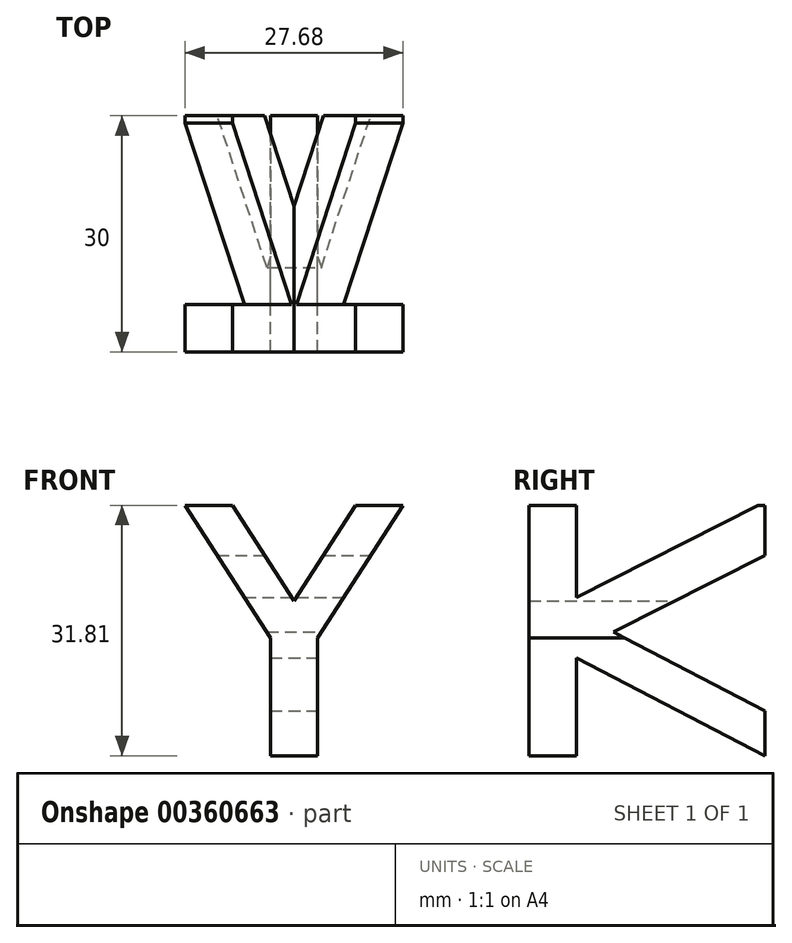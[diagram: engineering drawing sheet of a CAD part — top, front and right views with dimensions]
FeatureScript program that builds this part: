
annotation { "Feature Type Name" : "Feature", "Feature Type Description" : "" }
export const myFeature = defineFeature(function(context is Context, id is Id, definition is map)
    precondition{}
    {
        {
            var Q0;
            Q0=qCreatedBy(makeId("Front.planeOp"),FACE);
            var sketch = newSketch(context, id + "F0", { "sketchPlane" : qUnion([Q0])});
            skLineSegment(sketch, "E0", {"start": v(0, 0) * mm, "end": v(3, 0) * mm});
            skLineSegment(sketch, "E1", {"start": v(3, 0) * mm, "end": v(3, 15) * mm});
            skLineSegment(sketch, "E2", {"start": v(3, 15) * mm, "end": v(13.84, 31.8) * mm});
            skLineSegment(sketch, "E3", {"start": v(13.84, 31.8) * mm, "end": v(7.84, 31.8) * mm});
            skLineSegment(sketch, "E4", {"start": v(7.84, 31.8) * mm, "end": v(0, 19.65) * mm});
            skLineSegment(sketch, "E5.MirrorCS", {"start": v(-7.84, 31.8) * mm, "end": v(0, 19.65) * mm});
            skLineSegment(sketch, "E6.MirrorCS", {"start": v(-13.84, 31.8) * mm, "end": v(-7.84, 31.8) * mm});
            skLineSegment(sketch, "E7.MirrorCS", {"start": v(-3, 15) * mm, "end": v(-13.84, 31.8) * mm});
            skLineSegment(sketch, "E8.MirrorCS", {"start": v(-3, 0) * mm, "end": v(-3, 15) * mm});
            skLineSegment(sketch, "E9.MirrorCS", {"start": v(0, 0) * mm, "end": v(-3, 0) * mm});
            skSolve(sketch);
        }
        {
            var Q0;
            Q0=makeQuery(id+"F0.imprint","IMPRINT",FACE,{"disambiguationData":[TD([[makeQuery(id+"F0.imprint","IMPRINT",EDGE,{"derivedFrom":sQuery(id+"F0.wireOp",EDGE,"E0")}),1.0]])]});
            extrude(context, id + "F1", {"entities" : qUnion([Q0]), "depth" : 30 * mm});
        }
        {
            var Q0;
            Q0=qCreatedBy(makeId("Right.planeOp"),FACE);
            var sketch = newSketch(context, id + "F2", { "sketchPlane" : qUnion([Q0])});
            skLineSegment(sketch, "E10", {"start": v(0, 0) * mm, "end": v(-23.98, 12.43) * mm});
            skLineSegment(sketch, "E11", {"start": v(-23.98, 12.43) * mm, "end": v(-23.98, 0) * mm});
            skLineSegment(sketch, "E12", {"start": v(-23.98, 0) * mm, "end": v(0, 0) * mm});
            skLineSegment(sketch, "E13", {"start": v(0, 32.27) * mm, "end": v(-23.98, 32.27) * mm});
            skLineSegment(sketch, "E14", {"start": v(-23.98, 32.27) * mm, "end": v(-23.98, 20.13) * mm});
            skLineSegment(sketch, "E15", {"start": v(-23.98, 20.13) * mm, "end": v(0, 32.27) * mm});
            skLineSegment(sketch, "E16", {"start": v(0, 25.46) * mm, "end": v(-19.26, 15.71) * mm});
            skLineSegment(sketch, "E17", {"start": v(-19.26, 15.71) * mm, "end": v(0, 5.73) * mm});
            skLineSegment(sketch, "E18", {"start": v(0, 5.73) * mm, "end": v(0, 25.46) * mm});
            skSolve(sketch);
        }
        {
            var Q0;
            Q0=qSketchRegion(id+"F2",true);
            extrude(context, id + "F3", {"entities" : qUnion([Q0]), "operationType" : NewBodyOperationType.REMOVE, "endBound" : BoundingType.SYMMETRIC, "oppositeDirection" : true, "depth" : 100 * mm});
        }
    });
